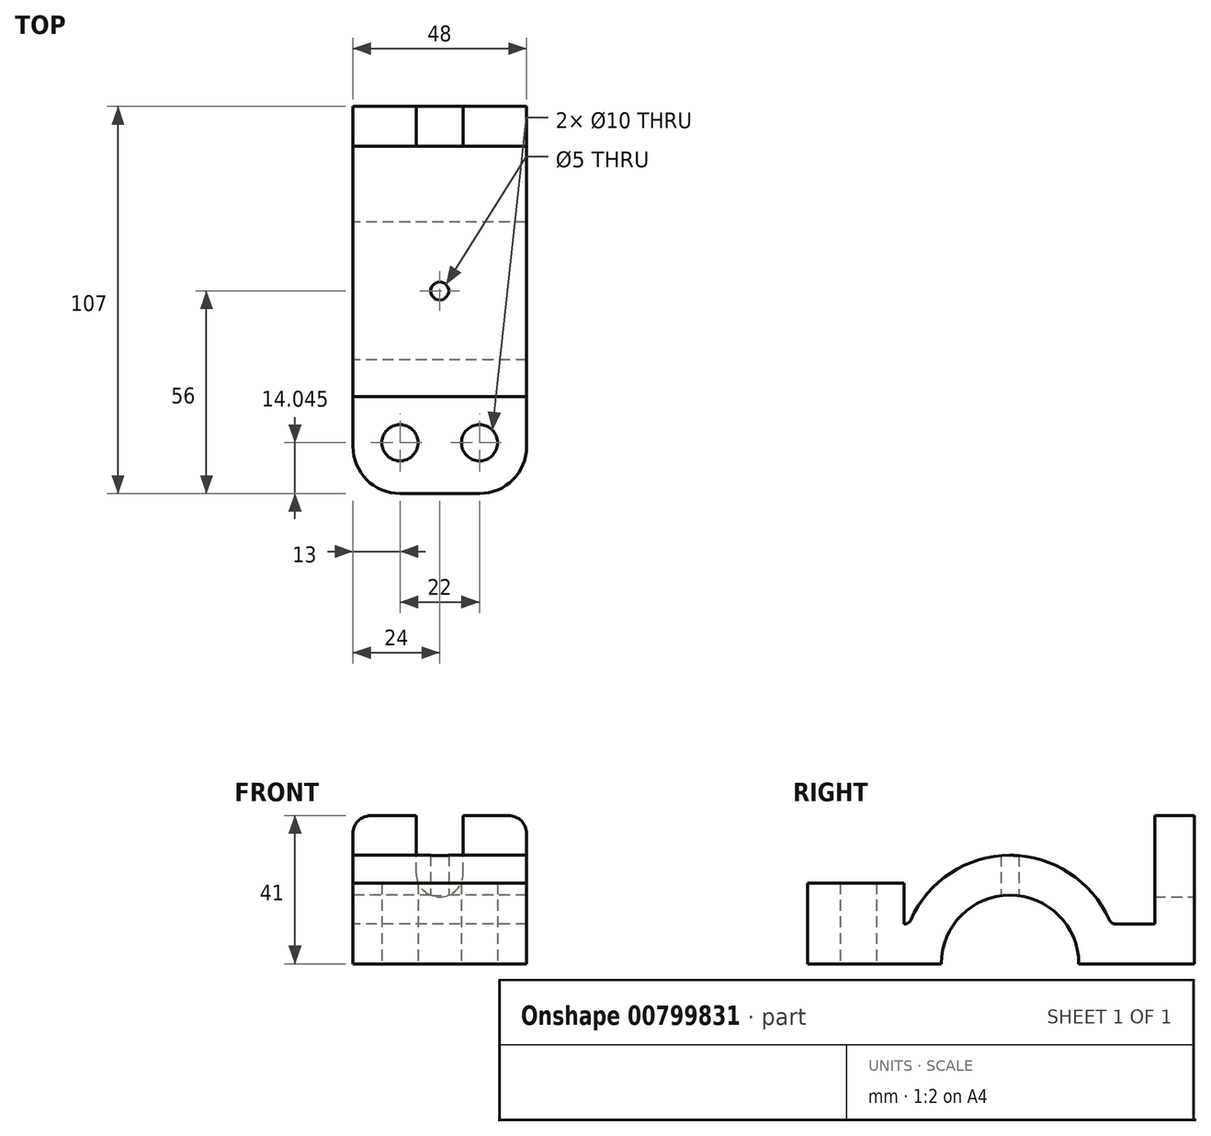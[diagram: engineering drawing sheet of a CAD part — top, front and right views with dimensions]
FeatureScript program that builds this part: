
annotation { "Feature Type Name" : "Feature", "Feature Type Description" : "" }
export const myFeature = defineFeature(function(context is Context, id is Id, definition is map)
    precondition{}
    {
        {
            var Q0;
            Q0=qCreatedBy(makeId("Right.planeOp"),FACE);
            var sketch = newSketch(context, id + "F0", { "sketchPlane" : qUnion([Q0])});
            skCircle(sketch, "E0", {"center": v(0, 0) * mm, "radius": 19 * mm});
            skCircle(sketch, "E1", {"center": v(0, 0) * mm, "radius": 30 * mm});
            skLineSegment(sketch, "E2.bottom", {"start": v(-56, 0) * mm, "end": v(51, 0) * mm});
            skLineSegment(sketch, "E2.top", {"start": v(-56, 11) * mm, "end": v(51, 11) * mm});
            skLineSegment(sketch, "E2.left", {"start": v(-56, 0) * mm, "end": v(-56, 11) * mm});
            skLineSegment(sketch, "E2.right", {"start": v(51, 0) * mm, "end": v(51, 11) * mm});
            skLineSegment(sketch, "E3.bottom", {"start": v(51, 11) * mm, "end": v(40, 11) * mm});
            skLineSegment(sketch, "E3.top", {"start": v(51, 41) * mm, "end": v(40, 41) * mm});
            skLineSegment(sketch, "E3.left", {"start": v(51, 11) * mm, "end": v(51, 41) * mm});
            skLineSegment(sketch, "E3.right", {"start": v(40, 11) * mm, "end": v(40, 41) * mm});
            skSolve(sketch);
        }
        {
            var Q0;
            {var subQ5=sQuery(id+"F0.wireOp",EDGE,"E2.left");Q0=makeQuery(id+"F0.imprint","IMPRINT",FACE,{"disambiguationData":[TD([[makeQuery(id+"F0.imprint","IMPRINT",EDGE,{"derivedFrom":subQ5}),-1.0]])]});}
            var Q1;
            {var subQ0=sQuery(id+"F0.wireOp",EDGE,"E2.bottom");var subQ1=sQuery(id+"F0.wireOp",EDGE,"E0");var subQ2=makeQuery(id+"F0.imprint","INTERSECT",VERTEX,{"disambiguationData":[OD(0.0)],"derivedFrom":[subQ1,subQ0]});Q1=makeQuery(id+"F0.imprint","IMPRINT",FACE,{"disambiguationData":[TD([[makeQuery(id+"F0.imprint","IMPRINT",EDGE,{"disambiguationData":[TD([[subQ2,1.0]])],"derivedFrom":subQ1}),-1.0]])]});}
            var Q2;
            {var subQ0=sQuery(id+"F0.wireOp",EDGE,"E2.top");var subQ1=sQuery(id+"F0.wireOp",EDGE,"E0");var subQ2=makeQuery(id+"F0.imprint","INTERSECT",VERTEX,{"disambiguationData":[OD(0.0)],"derivedFrom":[subQ1,subQ0]});Q2=makeQuery(id+"F0.imprint","IMPRINT",FACE,{"disambiguationData":[TD([[makeQuery(id+"F0.imprint","IMPRINT",EDGE,{"disambiguationData":[TD([[subQ2,1.0]])],"derivedFrom":subQ1}),-1.0]])]});}
            var Q3;
            {var subQ0=sQuery(id+"F0.wireOp",EDGE,"E2.top");var subQ1=sQuery(id+"F0.wireOp",EDGE,"E0");var subQ2=makeQuery(id+"F0.imprint","INTERSECT",VERTEX,{"disambiguationData":[OD(1.0)],"derivedFrom":[subQ1,subQ0]});Q3=makeQuery(id+"F0.imprint","IMPRINT",FACE,{"disambiguationData":[TD([[makeQuery(id+"F0.imprint","IMPRINT",EDGE,{"disambiguationData":[TD([[subQ2,1.0]])],"derivedFrom":subQ1}),-1.0]])]});}
            var Q4;
            {var subQ0=sQuery(id+"F0.wireOp",EDGE,"E2.right");Q4=makeQuery(id+"F0.imprint","IMPRINT",FACE,{"disambiguationData":[TD([[makeQuery(id+"F0.imprint","IMPRINT",EDGE,{"derivedFrom":subQ0}),1.0]])]});}
            var Q5;
            Q5=makeQuery(id+"F0.imprint","IMPRINT",FACE,{"disambiguationData":[TD([[makeQuery(id+"F0.imprint","IMPRINT",EDGE,{"derivedFrom":sQuery(id+"F0.wireOp",EDGE,"E3.top")}),1.0]])]});
            extrude(context, id + "F1", {"entities" : qUnion([Q0, Q1, Q2, Q3, Q4, Q5]), "endBound" : BoundingType.SYMMETRIC, "depth" : 48 * mm});
        }
        {
            var Q0;
            Q0=makeQuery(id+"F1.opExtrude","SWEPT_FACE",FACE,{"disambiguationData":[OSD([sQuery(id+"F0.wireOp",EDGE,"E2.right"),sQuery(id+"F0.wireOp",EDGE,"E3.left")])]});
            var sketch = newSketch(context, id + "F2", { "sketchPlane" : qUnion([Q0])});
            skLineSegment(sketch, "E4", {"start": v(0, 0) * mm, "end": v(0, 41) * mm, "construction": true});
            skCircle(sketch, "E5", {"center": v(0, 25) * mm, "radius": 6.5 * mm});
            skLineSegment(sketch, "E6", {"start": v(-6.5, 25) * mm, "end": v(-6.5, 41) * mm});
            skLineSegment(sketch, "E7", {"start": v(6.5, 25) * mm, "end": v(6.5, 41) * mm});
            skSolve(sketch);
        }
        {
            var Q0;
            {var subQ0=sQuery(id+"F2.wireOp",EDGE,"E5");var subQ2=makeQuery(id+"F2.imprint","INTERSECT",VERTEX,{"derivedFrom":[subQ0,sQuery(id+"F2.wireOp",EDGE,"E6")]});Q0=makeQuery(id+"F2.imprint","IMPRINT",FACE,{"disambiguationData":[TD([[makeQuery(id+"F2.imprint","IMPRINT",EDGE,{"disambiguationData":[TD([[subQ2,1.0]])],"derivedFrom":subQ0}),1.0]])]});}
            var Q1;
            {var subQ2=sQuery(id+"F2.wireOp",EDGE,"E6");Q1=makeQuery(id+"F2.imprint","IMPRINT",FACE,{"disambiguationData":[TD([[makeQuery(id+"F2.imprint","IMPRINT",EDGE,{"derivedFrom":subQ2}),-1.0]])]});}
            var Q2;
            Q2=makeQuery(id+"F1.opExtrude","SWEPT_FACE",FACE,{"disambiguationData":[OSD([sQuery(id+"F0.wireOp",EDGE,"E3.right")])]});
            extrude(context, id + "F3", {"entities" : qUnion([Q0, Q1]), "operationType" : NewBodyOperationType.REMOVE, "endBound" : BoundingType.UP_TO_SURFACE, "oppositeDirection" : true, "endBoundEntityFace" : qUnion([Q2]), "depth" : 25 * mm});
        }
        {
            var Q0;
            Q0=qCreatedBy(makeId("Top.planeOp"),FACE);
            var sketch = newSketch(context, id + "F4", { "sketchPlane" : qUnion([Q0])});
            skCircle(sketch, "E8", {"center": v(0, 0) * mm, "radius": 2.5 * mm});
            skLineSegment(sketch, "E9", {"start": v(24, -41.96) * mm, "end": v(-24, -41.96) * mm, "construction": true});
            skLineSegment(sketch, "E10", {"start": v(0, -56) * mm, "end": v(0, -27.91) * mm, "construction": true});
            skCircle(sketch, "E11", {"center": v(-11, -41.96) * mm, "radius": 5 * mm});
            skCircle(sketch, "E12", {"center": v(11, -41.96) * mm, "radius": 5 * mm});
            skSolve(sketch);
        }
        {
            var Q0;
            Q0=qSketchRegion(id+"F4",true);
            extrude(context, id + "F5", {"entities" : qUnion([Q0]), "operationType" : NewBodyOperationType.REMOVE, "endBound" : BoundingType.THROUGH_ALL, "depth" : 25 * mm});
        }
        {
            var Q0;
            Q0=makeQuery(id+"F1.opExtrude","CAP_EDGE",EDGE,{"disambiguationData":[OSD([sQuery(id+"F0.wireOp",EDGE,"E2.left")])],"isStart":false});
            var Q1;
            Q1=makeQuery(id+"F1.opExtrude","CAP_EDGE",EDGE,{"disambiguationData":[OSD([sQuery(id+"F0.wireOp",EDGE,"E2.left")])],"isStart":true});
            fillet(context, id + "F6", {"entities" : qUnion([Q0, Q1]), "radius" : 13 * mm, "tangentPropagation" : true, "allowEdgeOverflow" : false});
        }
        {
            var Q0;
            Q0=makeQuery(id+"F1.opExtrude","CAP_EDGE",EDGE,{"disambiguationData":[OSD([sQuery(id+"F0.wireOp",EDGE,"E3.top")])],"isStart":false});
            var Q1;
            Q1=makeQuery(id+"F1.opExtrude","CAP_EDGE",EDGE,{"disambiguationData":[OSD([sQuery(id+"F0.wireOp",EDGE,"E3.top")])],"isStart":true});
            fillet(context, id + "F7", {"entities" : qUnion([Q0, Q1]), "radius" : 5 * mm, "tangentPropagation" : true, "allowEdgeOverflow" : false});
        }
        {
            var Q0;
            {var subQ0=sQuery(id+"F0.wireOp",EDGE,"E2.top");var subQ1=sQuery(id+"F0.wireOp",EDGE,"E1");Q0=makeQuery(id+"F1.opExtrude","SWEPT_EDGE",EDGE,{"disambiguationData":[OSD([subQ1,subQ0]),TDD([makeQuery(id+"F0.imprint","INTERSECT",VERTEX,{"disambiguationData":[OD(1.0)],"derivedFrom":[subQ1,subQ0]})])]});}
            var Q1;
            {var subQ0=sQuery(id+"F0.wireOp",EDGE,"E2.top");var subQ1=sQuery(id+"F0.wireOp",EDGE,"E1");Q1=makeQuery(id+"F1.opExtrude","SWEPT_EDGE",EDGE,{"disambiguationData":[OSD([subQ1,subQ0]),TDD([makeQuery(id+"F0.imprint","INTERSECT",VERTEX,{"disambiguationData":[OD(0.0)],"derivedFrom":[subQ1,subQ0]})])]});}
            fillet(context, id + "F8", {"entities" : qUnion([Q0, Q1]), "radius" : 2 * mm, "tangentPropagation" : true, "allowEdgeOverflow" : false});
        }
        {
            var Q0;
            {var subQ0=sQuery(id+"F0.wireOp",EDGE,"E2.top");Q0=makeQuery(id+"F1.opExtrude","SWEPT_FACE",FACE,{"disambiguationData":[OSD([subQ0]),TDD([makeQuery(id+"F0.imprint","IMPRINT",EDGE,{"disambiguationData":[TD([[makeQuery(id+"F0.imprint","INTERSECT",VERTEX,{"derivedFrom":[subQ0,sQuery(id+"F0.wireOp",EDGE,"E2.left")]}),-1.0]])],"derivedFrom":subQ0})])]});}
            extrude(context, id + "F9", {"entities" : qUnion([Q0]), "operationType" : NewBodyOperationType.ADD, "depth" : 11.3 * mm, "offsetDistance" : 25 * mm});
        }
    });
